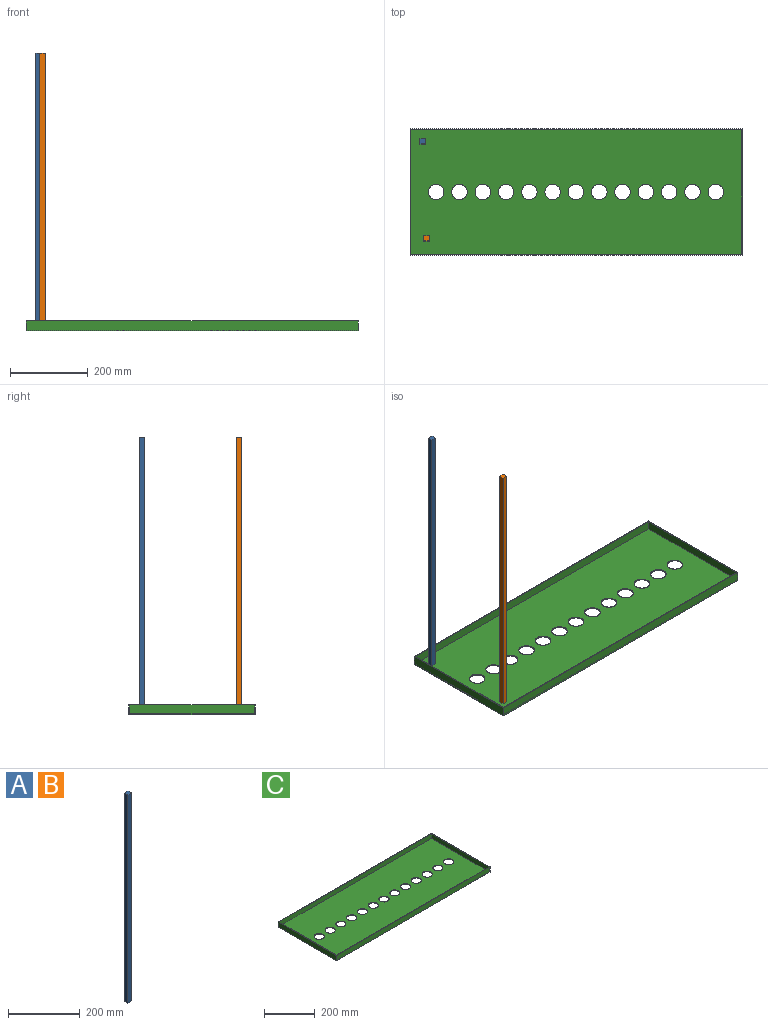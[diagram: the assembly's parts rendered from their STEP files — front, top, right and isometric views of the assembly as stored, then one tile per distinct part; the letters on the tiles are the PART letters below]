
ASSEMBLY  parts=3 mates=2
PART A: 6 faces, bbox 13.9x12.9x711.2 mm
  f0: plane 711.2x12.88mm, normal (1,0,0), area 9161.8mm2, adj f1,f3,f4,f5
  f1: plane 711.2x13.89mm, normal (0,1,0), area 9877.5mm2, adj f0,f2,f4,f5
  f2: plane 711.2x12.88mm, normal (-1,0,0), area 9161.8mm2, adj f1,f3,f4,f5
  f3: plane 711.2x13.89mm, normal (0,-1,0), area 9877.5mm2, adj f0,f2,f4,f5
  f4: plane 13.89x12.88mm, normal (0,0,-1), area 178.9mm2, adj f0,f1,f2,f3
  f5: plane 13.89x12.88mm, normal (0,0,1), area 178.9mm2, adj f0,f1,f2,f3
PART B: same geometry as A
PART C: 24 faces, bbox 855x325x25 mm
  f0: plane 855x325mm, normal (0,0,1), area 5875mm2, adj f1,f2,f3,f4,f6,f7,f8,f9
  f1: plane 855x25mm, normal (0,-1,0), area 21375mm2, adj f0,f2,f4,f5
  f2: plane 325x25mm, normal (1,0,0), area 8125mm2, adj f0,f1,f3,f5
  f3: plane 855x25mm, normal (0,1,0), area 21375mm2, adj f0,f2,f4,f5
  f4: plane 325x25mm, normal (-1,0,0), area 8125mm2, adj f0,f1,f3,f5
  f5: plane 855x325mm, normal (0,0,-1), area 261538.7mm2, adj f1,f2,f3,f4,f11,f12,f13,f14
  f6: plane 850x22.5mm, normal (0,1,0), area 19125mm2, adj f0,f7,f9,f10
  f7: plane 320x22.5mm, normal (-1,0,0), area 7200mm2, adj f0,f6,f8,f10
  f8: plane 850x22.5mm, normal (0,-1,0), area 19125mm2, adj f0,f7,f9,f10
  f9: plane 320x22.5mm, normal (1,0,0), area 7200mm2, adj f0,f6,f8,f10
  f10: plane 850x320mm, normal (0,0,1), area 255663.7mm2, adj f6,f7,f8,f9,f11,f12,f13,f14
  f11: cylinder r=20mm len=40mm, axis (0,0,1), area 314.2mm2, adj f5,f10
  f12: cylinder r=20mm len=40mm, axis (0,0,1), area 314.2mm2, adj f5,f10
  f13: cylinder r=20mm len=40mm, axis (0,0,1), area 314.2mm2, adj f5,f10
  f14: cylinder r=20mm len=40mm, axis (0,0,1), area 314.2mm2, adj f5,f10
  f15: cylinder r=20mm len=40mm, axis (0,0,1), area 314.2mm2, adj f5,f10
  f16: cylinder r=20mm len=40mm, axis (0,0,1), area 314.2mm2, adj f5,f10
  f17: cylinder r=20mm len=40mm, axis (0,0,1), area 314.2mm2, adj f5,f10
  f18: cylinder r=20mm len=40mm, axis (0,0,1), area 314.2mm2, adj f5,f10
  f19: cylinder r=20mm len=40mm, axis (0,0,1), area 314.2mm2, adj f5,f10
  f20: cylinder r=20mm len=40mm, axis (0,0,1), area 314.2mm2, adj f5,f10
  f21: cylinder r=20mm len=40mm, axis (0,0,1), area 314.2mm2, adj f5,f10
  f22: cylinder r=20mm len=40mm, axis (0,0,1), area 314.2mm2, adj f5,f10
  f23: cylinder r=20mm len=40mm, axis (0,0,1), area 314.2mm2, adj f5,f10
PLACE A t=(-737.81,126.72,695.94)mm
PLACE B t=(-727.81,-123.28,695.94)mm
PLACE C t=(-342.81,-3.28,-17.76)mm
MATE fastened A.f4 <-> C.f10  axis (0,0,-1) through (-737.81,126.72,-15.26)mm
MATE fastened B.f4 <-> C.f10  axis (0,0,-1) through (-727.81,-123.28,-15.26)mm
